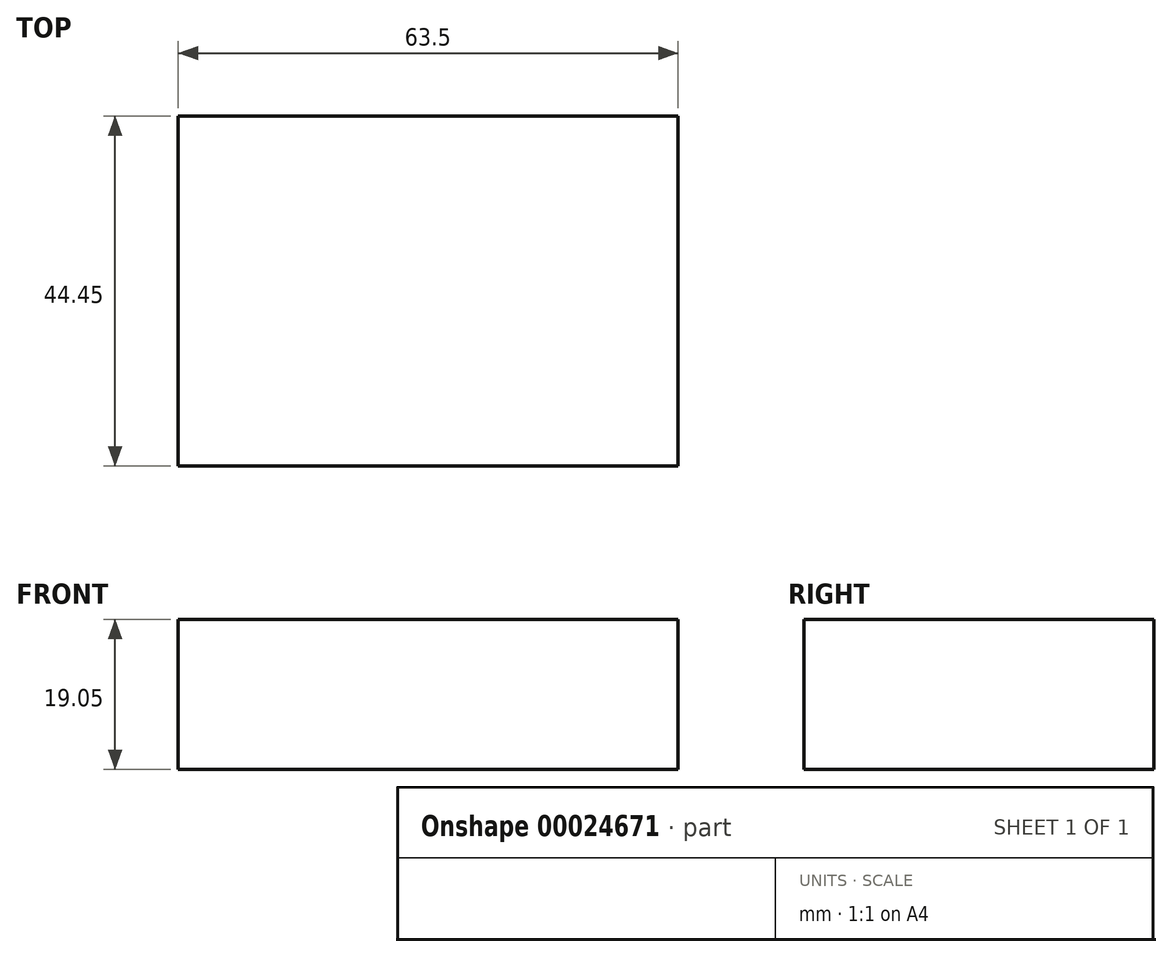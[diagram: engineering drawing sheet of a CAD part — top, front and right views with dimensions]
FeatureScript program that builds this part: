
annotation { "Feature Type Name" : "Feature", "Feature Type Description" : "" }
export const myFeature = defineFeature(function(context is Context, id is Id, definition is map)
    precondition{}
    {
        {
            var Q0;
            Q0=qCreatedBy(makeId("Top.planeOp"),FACE);
            var sketch = newSketch(context, id + "F0", { "sketchPlane" : qUnion([Q0])});
            skLineSegment(sketch, "E0.bottom", {"start": v(-43.65, 22.47) * mm, "end": v(19.85, 22.47) * mm});
            skLineSegment(sketch, "E0.top", {"start": v(-43.65, -21.98) * mm, "end": v(19.85, -21.98) * mm});
            skLineSegment(sketch, "E0.left", {"start": v(-43.65, 22.47) * mm, "end": v(-43.65, -21.98) * mm});
            skLineSegment(sketch, "E0.right", {"start": v(19.85, 22.47) * mm, "end": v(19.85, -21.98) * mm});
            skSolve(sketch);
        }
        {
            var Q0;
            Q0 = qSketchRegion(id + "F0", true);
            extrude(context, id + "F1", {"entities" : qUnion([Q0]), "depth" : 19.05 * mm});
        }
    });
